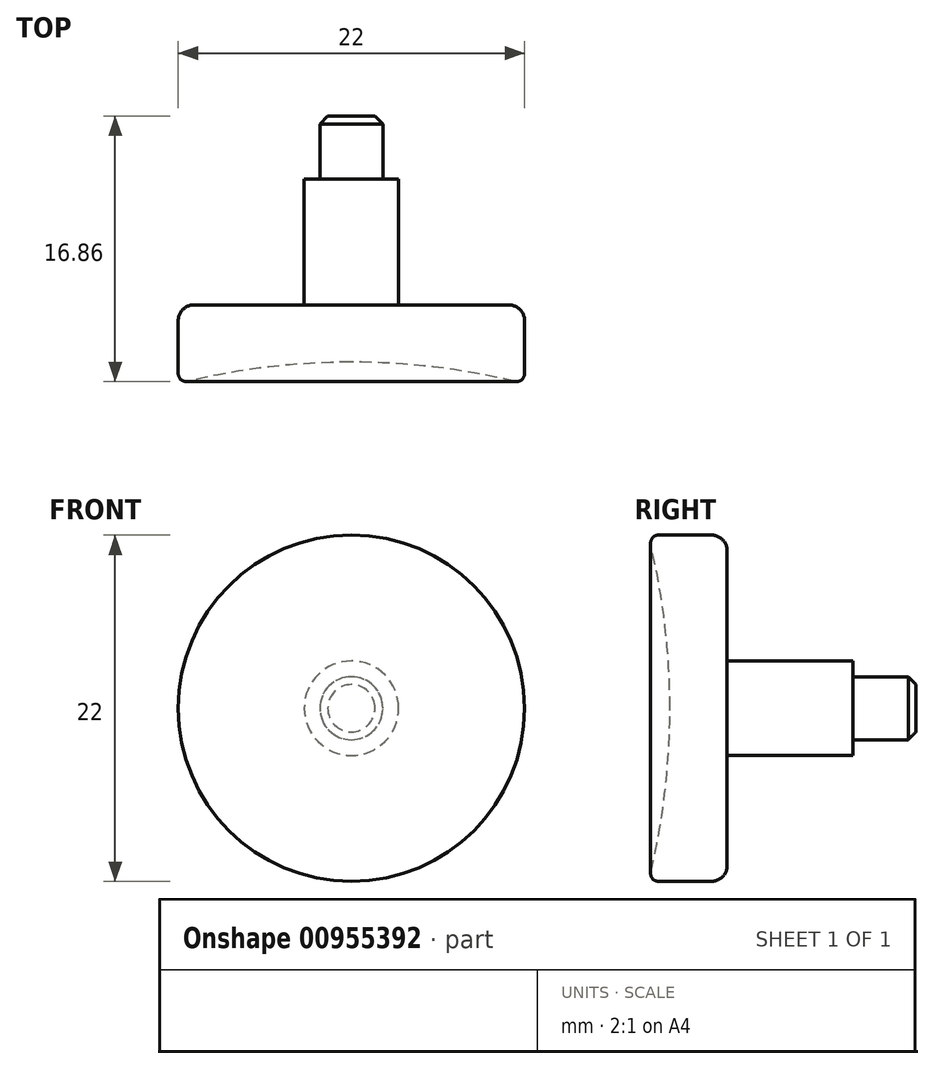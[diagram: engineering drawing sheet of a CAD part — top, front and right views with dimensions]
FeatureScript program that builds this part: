
annotation { "Feature Type Name" : "Feature", "Feature Type Description" : "" }
export const myFeature = defineFeature(function(context is Context, id is Id, definition is map)
    precondition{}
    {
        {
            var Q0;
            Q0=qCreatedBy(makeId("Right.planeOp"),FACE);
            var sketch = newSketch(context, id + "F0", { "sketchPlane" : qUnion([Q0])});
            skLineSegment(sketch, "E0", {"start": v(8.63, 11) * mm, "end": v(8.63, 3) * mm});
            skLineSegment(sketch, "E1", {"start": v(8.63, 3) * mm, "end": v(16.63, 3) * mm});
            skLineSegment(sketch, "E2", {"start": v(16.63, 3) * mm, "end": v(16.63, 2) * mm});
            skLineSegment(sketch, "E3", {"start": v(16.63, 2) * mm, "end": v(20.63, 2) * mm});
            skLineSegment(sketch, "E4", {"start": v(20.63, 2) * mm, "end": v(20.63, 0) * mm});
            skArc(sketch, "E5", {"start": v(5, 0) * mm, "mid": v(4.66, 5.54) * mm, "end": v(3.63, 11) * mm});
            skLineSegment(sketch, "E6", {"start": v(8.63, 11) * mm, "end": v(3.63, 11) * mm});
            skLineSegment(sketch, "E7", {"start": v(20.63, 0) * mm, "end": v(5, 0) * mm});
            skSolve(sketch);
        }
        {
            var Q0;
            Q0=qSketchRegion(id+"F0",true);
            var Q1;
            Q1=sQuery(id+"F0.wireOp",EDGE,"E7");
            revolve(context, id + "F1", {"entities" : qUnion([Q0]), "axis" : qUnion([Q1]), "revolveType" : RevolveType.FULL});
        }
        {
            var Q0;
            Q0=makeQuery(id+"F1.opRevolve","SWEPT_EDGE",EDGE,{"disambiguationData":[OSD([sQuery(id+"F0.wireOp",EDGE,"E3"),sQuery(id+"F0.wireOp",EDGE,"E4")])]});
            chamfer(context, id + "F2", {"entities" : qUnion([Q0]), "width" : 0.5 * mm, "tangentPropagation" : true});
        }
        {
            var Q0;
            Q0=makeQuery(id+"F1.opRevolve","SWEPT_EDGE",EDGE,{"disambiguationData":[OSD([sQuery(id+"F0.wireOp",EDGE,"E0"),sQuery(id+"F0.wireOp",EDGE,"E6")])]});
            fillet(context, id + "F3", {"entities" : qUnion([Q0]), "radius" : 1 * mm, "tangentPropagation" : true, "allowEdgeOverflow" : false});
        }
        {
            var Q0;
            Q0=makeQuery(id+"F1.opRevolve","SWEPT_EDGE",EDGE,{"disambiguationData":[OSD([sQuery(id+"F0.wireOp",EDGE,"E5"),sQuery(id+"F0.wireOp",EDGE,"E6")])]});
            fillet(context, id + "F4", {"entities" : qUnion([Q0]), "radius" : 0.5 * mm, "tangentPropagation" : true, "allowEdgeOverflow" : false});
        }
    });
